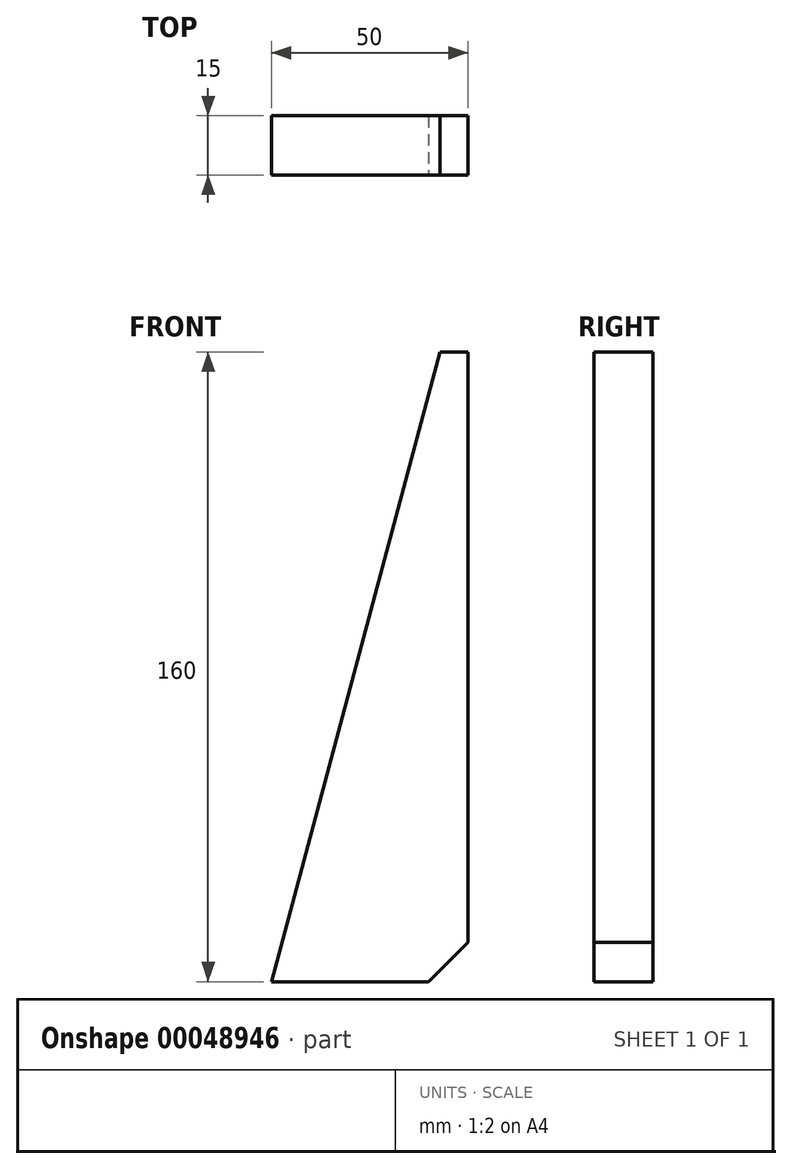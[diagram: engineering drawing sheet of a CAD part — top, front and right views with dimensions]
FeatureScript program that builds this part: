
annotation { "Feature Type Name" : "Feature", "Feature Type Description" : "" }
export const myFeature = defineFeature(function(context is Context, id is Id, definition is map)
    precondition{}
    {
        {
            var Q0;
            Q0=qCreatedBy(makeId("Front.planeOp"),FACE);
            var sketch = newSketch(context, id + "F0", { "sketchPlane" : qUnion([Q0])});
            skLineSegment(sketch, "E0", {"start": v(0, 0) * mm, "end": v(-50, 0) * mm});
            skLineSegment(sketch, "E1", {"start": v(0, 0) * mm, "end": v(0, 160) * mm});
            skLineSegment(sketch, "E2", {"start": v(0, 160) * mm, "end": v(-7.13, 160) * mm});
            skLineSegment(sketch, "E3", {"start": v(-7.13, 160) * mm, "end": v(-50, 0) * mm});
            skSolve(sketch);
        }
        {
            var Q0;
            Q0=makeQuery(id+"F0.imprint","IMPRINT",FACE,{"disambiguationData":[TD([[makeQuery(id+"F0.imprint","IMPRINT",EDGE,{"derivedFrom":sQuery(id+"F0.wireOp",EDGE,"E0")}),-1.0]])]});
            extrude(context, id + "F1", {"entities" : qUnion([Q0]), "depth" : 15 * mm});
        }
        {
            var Q0;
            Q0=makeQuery(id+"F1.opExtrude","SWEPT_EDGE",EDGE,{"disambiguationData":[OSD([sQuery(id+"F0.wireOp",EDGE,"E0"),sQuery(id+"F0.wireOp",EDGE,"E1")])]});
            chamfer(context, id + "F2", {"entities" : qUnion([Q0]), "chamferType" : ChamferType.OFFSET_ANGLE, "width" : 10 * mm, "oppositeDirection" : false, "angle" : 45 * degree, "tangentPropagation" : true});
        }
    });
